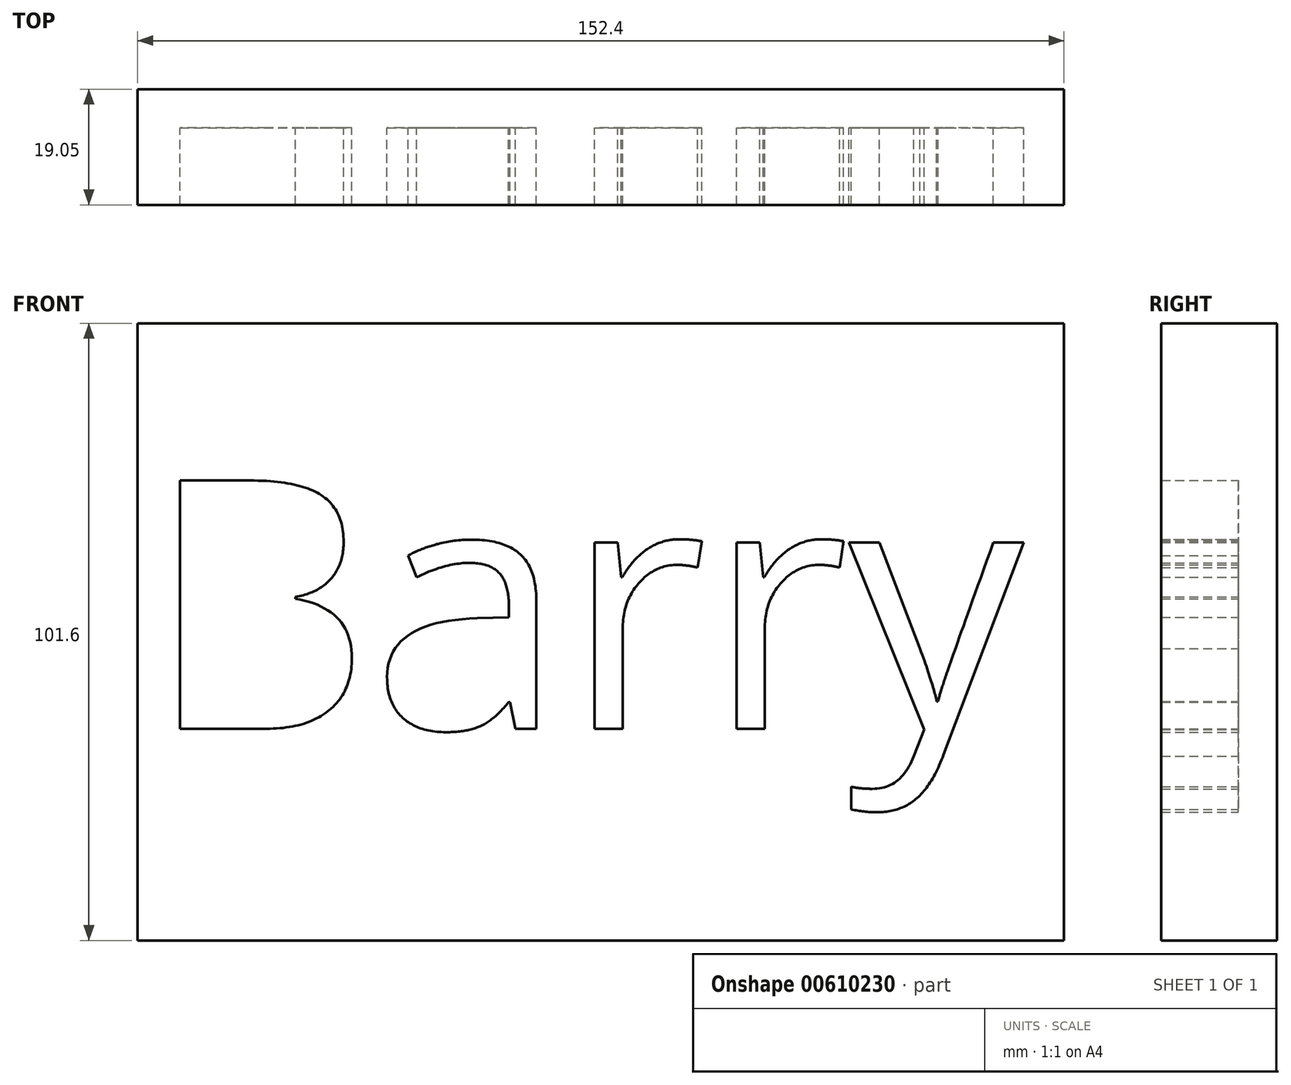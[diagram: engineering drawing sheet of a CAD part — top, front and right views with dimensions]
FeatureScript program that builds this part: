
annotation { "Feature Type Name" : "Feature", "Feature Type Description" : "" }
export const myFeature = defineFeature(function(context is Context, id is Id, definition is map)
    precondition{}
    {
        {
            var Q0;
            Q0=qCreatedBy(makeId("Front.planeOp"),FACE);
            var sketch = newSketch(context, id + "F0", { "sketchPlane" : qUnion([Q0])});
            skLineSegment(sketch, "E0.bottom", {"start": v(-149.48, 129.7) * mm, "end": v(2.92, 129.7) * mm});
            skLineSegment(sketch, "E0.top", {"start": v(-149.48, 28.1) * mm, "end": v(2.92, 28.1) * mm});
            skLineSegment(sketch, "E0.left", {"start": v(-149.48, 129.7) * mm, "end": v(-149.48, 28.1) * mm});
            skLineSegment(sketch, "E0.right", {"start": v(2.92, 129.7) * mm, "end": v(2.92, 28.1) * mm});
            skSolve(sketch);
        }
        {
            var Q0;
            Q0=makeQuery(id+"F0.imprint","IMPRINT",FACE,{"disambiguationData":[TD([[makeQuery(id+"F0.imprint","IMPRINT",EDGE,{"derivedFrom":sQuery(id+"F0.wireOp",EDGE,"E0.bottom")}),-1.0]])]});
            extrude(context, id + "F1", {"entities" : qUnion([Q0]), "depth" : 6.35 * mm, "offsetDistance" : 25.4 * mm});
        }
        {
            var Q0;
            Q0=makeQuery(id+"F1.opExtrude","CAP_FACE",FACE,{"disambiguationData":[OSD([sQuery(id+"F0.wireOp",EDGE,"E0.bottom"),sQuery(id+"F0.wireOp",EDGE,"E0.top"),sQuery(id+"F0.wireOp",EDGE,"E0.left"),sQuery(id+"F0.wireOp",EDGE,"E0.right")])],"isStart":false});
            var sketch = newSketch(context, id + "F2", { "sketchPlane" : qUnion([Q0])});
            skText(sketch, "E1", { "text": "Barry", "fontName": "OpenSans-Regular.ttf"});
            const initialGuessF2  = {"E1": [-0.14816, 0.06296, 1, 0, 0.04121]};
            skSetInitialGuess(sketch, initialGuessF2);
            skSolve(sketch);
        }
        {
            var Q0;
            Q0=makeQuery(id+"F2.imprint","IMPRINT",FACE,{"disambiguationData":[TD([[makeQuery(id+"F2.imprint","IMPRINT",EDGE,{"derivedFrom":sQuery(id+"F2.wireOp",EDGE,"E1.sketch_text.stroke-0")}),1.0]])]});
            extrude(context, id + "F3", {"entities" : qUnion([Q0]), "operationType" : NewBodyOperationType.ADD, "depth" : 12.7 * mm, "offsetDistance" : 25.4 * mm});
        }
    });
